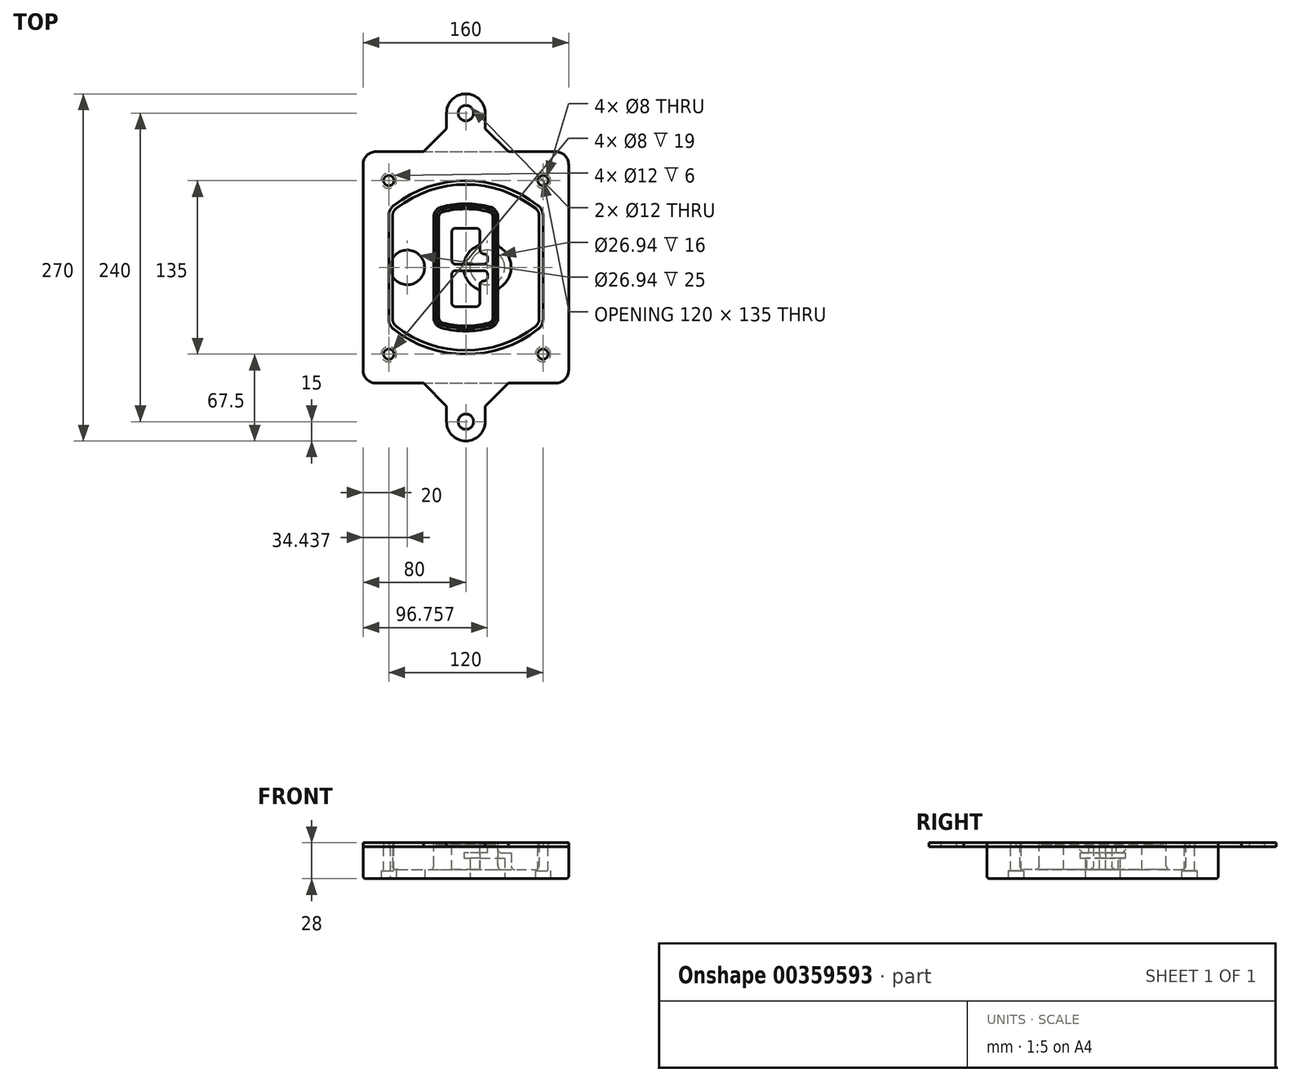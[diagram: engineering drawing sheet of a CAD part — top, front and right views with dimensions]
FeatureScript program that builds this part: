
annotation { "Feature Type Name" : "Feature", "Feature Type Description" : "" }
export const myFeature = defineFeature(function(context is Context, id is Id, definition is map)
    precondition{}
    {
        {
            var Q0;
            Q0=qCreatedBy(makeId("Top.planeOp"),FACE);
            var sketch = newSketch(context, id + "F0", { "sketchPlane" : qUnion([Q0])});
            skPoint(sketch, "E0.rect.middle", {"position": v(0, 0) * mm});
            skLineSegment(sketch, "E1.bottom", {"start": v(-70, -90) * mm, "end": v(70, -90) * mm});
            skLineSegment(sketch, "E1.top", {"start": v(-70, 90) * mm, "end": v(70, 90) * mm});
            skLineSegment(sketch, "E1.left", {"start": v(-80, -80) * mm, "end": v(-80, 80) * mm});
            skLineSegment(sketch, "E1.right", {"start": v(80, -80) * mm, "end": v(80, 80) * mm});
            skLineSegment(sketch, "E2", {"start": v(-80, 90) * mm, "end": v(80, -90) * mm, "construction": true});
            skLineSegment(sketch, "E3", {"start": v(80, 90) * mm, "end": v(-80, -90) * mm, "construction": true});
            skCircle(sketch, "E4", {"center": v(-60, 67.5) * mm, "radius": 4 * mm});
            skCircle(sketch, "E5", {"center": v(60, 67.5) * mm, "radius": 4 * mm});
            skCircle(sketch, "E6", {"center": v(60, -67.5) * mm, "radius": 4 * mm});
            skCircle(sketch, "E7", {"center": v(-60, -67.5) * mm, "radius": 4 * mm});
            skLineSegment(sketch, "E8", {"start": v(-60, 67.5) * mm, "end": v(60, 67.5) * mm, "construction": true});
            skLineSegment(sketch, "E9", {"start": v(60, 67.5) * mm, "end": v(60, -67.5) * mm, "construction": true});
            skLineSegment(sketch, "E10", {"start": v(60, -67.5) * mm, "end": v(-60, -67.5) * mm, "construction": true});
            skLineSegment(sketch, "E11", {"start": v(-60, -67.5) * mm, "end": v(-60, 67.5) * mm, "construction": true});
            skLineSegment(sketch, "E12", {"start": v(-60, 40.3) * mm, "end": v(-60, -40.3) * mm});
            skLineSegment(sketch, "E13", {"start": v(60, 40.3) * mm, "end": v(60, -40.3) * mm});
            skArc(sketch, "E14", {"start": v(56.15, 48.18) * mm, "mid": v(0, 67.5) * mm, "end": v(-56.15, 48.18) * mm});
            skArc(sketch, "E15", {"start": v(-56.15, -48.18) * mm, "mid": v(0, -67.5) * mm, "end": v(56.15, -48.18) * mm});
            skLineSegment(sketch, "E16", {"start": v(-60, 0) * mm, "end": v(60, 0) * mm, "construction": true});
            skPoint(sketch, "E17.visualSharp", {"position": v(-60, -45) * mm});
            skArc(sketch, "E17.filletArc", {"start": v(-60, -40.3) * mm, "mid": v(-58.99, -44.68) * mm, "end": v(-56.15, -48.18) * mm});
            skPoint(sketch, "E18.visualSharp", {"position": v(-60, 45) * mm});
            skArc(sketch, "E18.filletArc", {"start": v(-56.15, 48.18) * mm, "mid": v(-58.99, 44.68) * mm, "end": v(-60, 40.3) * mm});
            skPoint(sketch, "E19.visualSharp", {"position": v(60, 45) * mm});
            skArc(sketch, "E19.filletArc", {"start": v(60, 40.3) * mm, "mid": v(58.99, 44.68) * mm, "end": v(56.15, 48.18) * mm});
            skPoint(sketch, "E20.visualSharp", {"position": v(60, -45) * mm});
            skArc(sketch, "E20.filletArc", {"start": v(56.15, -48.18) * mm, "mid": v(58.99, -44.68) * mm, "end": v(60, -40.3) * mm});
            skPoint(sketch, "E21.visualSharp", {"position": v(-80, 90) * mm});
            skArc(sketch, "E21.filletArc", {"start": v(-70, 90) * mm, "mid": v(-77.07, 87.07) * mm, "end": v(-80, 80) * mm});
            skPoint(sketch, "E22.visualSharp", {"position": v(80, 90) * mm});
            skArc(sketch, "E22.filletArc", {"start": v(80, 80) * mm, "mid": v(77.07, 87.07) * mm, "end": v(70, 90) * mm});
            skPoint(sketch, "E23.visualSharp", {"position": v(80, -90) * mm});
            skArc(sketch, "E23.filletArc", {"start": v(70, -90) * mm, "mid": v(77.07, -87.07) * mm, "end": v(80, -80) * mm});
            skPoint(sketch, "E24.visualSharp", {"position": v(-80, -90) * mm});
            skArc(sketch, "E24.filletArc", {"start": v(-80, -80) * mm, "mid": v(-77.07, -87.07) * mm, "end": v(-70, -90) * mm});
            skArc(sketch, "E25.0", {"start": v(57, 40.3) * mm, "mid": v(56.3, 43.36) * mm, "end": v(54.3, 45.81) * mm});
            skLineSegment(sketch, "E25.1", {"start": v(57, 40.3) * mm, "end": v(57, -40.3) * mm});
            skArc(sketch, "E25.2", {"start": v(54.3, -45.81) * mm, "mid": v(56.3, -43.36) * mm, "end": v(57, -40.3) * mm});
            skArc(sketch, "E25.3", {"start": v(-54.3, -45.81) * mm, "mid": v(0, -64.5) * mm, "end": v(54.3, -45.81) * mm});
            skArc(sketch, "E25.4", {"start": v(-57, -40.3) * mm, "mid": v(-56.3, -43.36) * mm, "end": v(-54.3, -45.81) * mm});
            skArc(sketch, "E25.5", {"start": v(54.3, 45.81) * mm, "mid": v(0, 64.5) * mm, "end": v(-54.3, 45.81) * mm});
            skLineSegment(sketch, "E25.6", {"start": v(-57, 40.3) * mm, "end": v(-57, -40.3) * mm});
            skArc(sketch, "E25.7", {"start": v(-54.3, 45.81) * mm, "mid": v(-56.3, 43.36) * mm, "end": v(-57, 40.3) * mm});
            skArc(sketch, "E26.0", {"start": v(-58.62, 51.33) * mm, "mid": v(-62.58, 46.43) * mm, "end": v(-64, 40.3) * mm});
            skArc(sketch, "E26.1", {"start": v(58.62, 51.33) * mm, "mid": v(0, 71.5) * mm, "end": v(-58.62, 51.33) * mm});
            skArc(sketch, "E26.2", {"start": v(64, 40.3) * mm, "mid": v(62.58, 46.43) * mm, "end": v(58.62, 51.33) * mm});
            skLineSegment(sketch, "E26.3", {"start": v(64, 40.3) * mm, "end": v(64, -40.3) * mm});
            skArc(sketch, "E26.4", {"start": v(58.62, -51.33) * mm, "mid": v(62.58, -46.43) * mm, "end": v(64, -40.3) * mm});
            skLineSegment(sketch, "E26.5", {"start": v(-64, 40.3) * mm, "end": v(-64, -40.3) * mm});
            skArc(sketch, "E26.6", {"start": v(-58.62, -51.33) * mm, "mid": v(0, -71.5) * mm, "end": v(58.62, -51.33) * mm});
            skArc(sketch, "E26.7", {"start": v(-64, -40.3) * mm, "mid": v(-62.58, -46.43) * mm, "end": v(-58.62, -51.33) * mm});
            skSolve(sketch);
        }
        {
            var Q0;
            Q0=makeQuery(id+"F0.imprint","IMPRINT",FACE,{"disambiguationData":[TD([[makeQuery(id+"F0.imprint","IMPRINT",EDGE,{"derivedFrom":sQuery(id+"F0.wireOp",EDGE,"E1.bottom")}),1.0]])]});
            var Q1;
            Q1=makeQuery(id+"F0.imprint","IMPRINT",FACE,{"disambiguationData":[TD([[makeQuery(id+"F0.imprint","IMPRINT",EDGE,{"derivedFrom":sQuery(id+"F0.wireOp",EDGE,"E12")}),1.0]])]});
            var Q2;
            Q2=makeQuery(id+"F0.imprint","IMPRINT",FACE,{"disambiguationData":[TD([[makeQuery(id+"F0.imprint","IMPRINT",EDGE,{"derivedFrom":sQuery(id+"F0.wireOp",EDGE,"E25.0")}),1.0]])]});
            var Q3;
            Q3=makeQuery(id+"F0.imprint","IMPRINT",FACE,{"disambiguationData":[TD([[makeQuery(id+"F0.imprint","IMPRINT",EDGE,{"derivedFrom":sQuery(id+"F0.wireOp",EDGE,"E12")}),-1.0]])]});
            extrude(context, id + "F1", {"entities" : qUnion([Q0, Q1, Q2, Q3]), "oppositeDirection" : true, "depth" : 25 * mm});
        }
        {
            var Q0;
            Q0=makeQuery(id+"F0.imprint","IMPRINT",FACE,{"disambiguationData":[TD([[makeQuery(id+"F0.imprint","IMPRINT",EDGE,{"derivedFrom":sQuery(id+"F0.wireOp",EDGE,"E12")}),1.0]])]});
            extrude(context, id + "F2", {"entities" : qUnion([Q0]), "operationType" : NewBodyOperationType.ADD, "depth" : 3 * mm});
        }
        {
            var Q0;
            Q0=makeQuery(id+"F0.imprint","IMPRINT",FACE,{"disambiguationData":[TD([[makeQuery(id+"F0.imprint","IMPRINT",EDGE,{"derivedFrom":sQuery(id+"F0.wireOp",EDGE,"E25.0")}),1.0]])]});
            extrude(context, id + "F3", {"entities" : qUnion([Q0]), "operationType" : NewBodyOperationType.REMOVE, "oppositeDirection" : true, "depth" : 18 * mm});
        }
        {
            var Q0;
            Q0=makeQuery(id+"F2.opExtrude","CAP_FACE",FACE,{"disambiguationData":[OSD([sQuery(id+"F0.wireOp",EDGE,"E12"),sQuery(id+"F0.wireOp",EDGE,"E13"),sQuery(id+"F0.wireOp",EDGE,"E14"),sQuery(id+"F0.wireOp",EDGE,"E15"),sQuery(id+"F0.wireOp",EDGE,"E17.filletArc"),sQuery(id+"F0.wireOp",EDGE,"E18.filletArc"),sQuery(id+"F0.wireOp",EDGE,"E19.filletArc"),sQuery(id+"F0.wireOp",EDGE,"E20.filletArc"),sQuery(id+"F0.wireOp",EDGE,"E25.0"),sQuery(id+"F0.wireOp",EDGE,"E25.1"),sQuery(id+"F0.wireOp",EDGE,"E25.2"),sQuery(id+"F0.wireOp",EDGE,"E25.3"),sQuery(id+"F0.wireOp",EDGE,"E25.4"),sQuery(id+"F0.wireOp",EDGE,"E25.5"),sQuery(id+"F0.wireOp",EDGE,"E25.6"),sQuery(id+"F0.wireOp",EDGE,"E25.7")])],"isStart":false});
            var sketch = newSketch(context, id + "F4", { "sketchPlane" : qUnion([Q0])});
            skArc(sketch, "E27.0", {"start": v(-19.08, -46.97) * mm, "mid": v(0, -49.5) * mm, "end": v(19.08, -46.97) * mm});
            skArc(sketch, "E28.0", {"start": v(19.08, 46.97) * mm, "mid": v(0, 49.5) * mm, "end": v(-19.08, 46.97) * mm});
            skLineSegment(sketch, "E29", {"start": v(-25, 39.25) * mm, "end": v(-25, -39.25) * mm});
            skLineSegment(sketch, "E30", {"start": v(25, 39.25) * mm, "end": v(25, -39.25) * mm});
            skLineSegment(sketch, "E31", {"start": v(-25, 45.1) * mm, "end": v(25, 45.1) * mm, "construction": true});
            skLineSegment(sketch, "E32", {"start": v(-25, -45.1) * mm, "end": v(25, -45.1) * mm, "construction": true});
            skPoint(sketch, "E33.visualSharp", {"position": v(-25, 45.1) * mm});
            skArc(sketch, "E33.filletArc", {"start": v(-19.08, 46.97) * mm, "mid": v(-23.35, 44.11) * mm, "end": v(-25, 39.25) * mm});
            skPoint(sketch, "E34.visualSharp", {"position": v(25, 45.1) * mm});
            skArc(sketch, "E34.filletArc", {"start": v(25, 39.25) * mm, "mid": v(23.35, 44.11) * mm, "end": v(19.08, 46.97) * mm});
            skPoint(sketch, "E35.visualSharp", {"position": v(25, -45.1) * mm});
            skArc(sketch, "E35.filletArc", {"start": v(19.08, -46.97) * mm, "mid": v(23.35, -44.11) * mm, "end": v(25, -39.25) * mm});
            skPoint(sketch, "E36.visualSharp", {"position": v(-25, -45.1) * mm});
            skArc(sketch, "E36.filletArc", {"start": v(-25, -39.25) * mm, "mid": v(-23.35, -44.11) * mm, "end": v(-19.08, -46.97) * mm});
            skArc(sketch, "E37.0", {"start": v(54.3, 45.81) * mm, "mid": v(0, 64.5) * mm, "end": v(-54.3, 45.81) * mm});
            skArc(sketch, "E37.1", {"start": v(-54.3, 45.81) * mm, "mid": v(-56.3, 43.36) * mm, "end": v(-57, 40.3) * mm});
            skLineSegment(sketch, "E37.2", {"start": v(-57, 40.3) * mm, "end": v(-57, -40.3) * mm});
            skArc(sketch, "E37.3", {"start": v(-57, -40.3) * mm, "mid": v(-56.3, -43.36) * mm, "end": v(-54.3, -45.81) * mm});
            skArc(sketch, "E37.4", {"start": v(-54.3, -45.81) * mm, "mid": v(0, -64.5) * mm, "end": v(54.3, -45.81) * mm});
            skArc(sketch, "E37.5", {"start": v(54.3, -45.81) * mm, "mid": v(56.3, -43.36) * mm, "end": v(57, -40.3) * mm});
            skLineSegment(sketch, "E37.6", {"start": v(57, 40.3) * mm, "end": v(57, -40.3) * mm});
            skArc(sketch, "E37.7", {"start": v(57, 40.3) * mm, "mid": v(56.3, 43.36) * mm, "end": v(54.3, 45.81) * mm});
            skLineSegment(sketch, "E38.0", {"start": v(23, 39.25) * mm, "end": v(23, -39.25) * mm});
            skArc(sketch, "E38.1", {"start": v(18.56, -45.04) * mm, "mid": v(21.76, -42.9) * mm, "end": v(23, -39.25) * mm});
            skArc(sketch, "E38.2", {"start": v(-18.56, -45.04) * mm, "mid": v(0, -47.5) * mm, "end": v(18.56, -45.04) * mm});
            skArc(sketch, "E38.3", {"start": v(-23, -39.25) * mm, "mid": v(-21.76, -42.9) * mm, "end": v(-18.56, -45.04) * mm});
            skLineSegment(sketch, "E38.4", {"start": v(-23, 39.25) * mm, "end": v(-23, -39.25) * mm});
            skArc(sketch, "E38.5", {"start": v(23, 39.25) * mm, "mid": v(21.76, 42.9) * mm, "end": v(18.56, 45.04) * mm});
            skArc(sketch, "E38.6", {"start": v(-18.56, 45.04) * mm, "mid": v(-21.76, 42.9) * mm, "end": v(-23, 39.25) * mm});
            skArc(sketch, "E38.7", {"start": v(18.56, 45.04) * mm, "mid": v(0, 47.5) * mm, "end": v(-18.56, 45.04) * mm});
            skArc(sketch, "E39.0", {"start": v(21, 39.25) * mm, "mid": v(20.18, 41.68) * mm, "end": v(18.04, 43.1) * mm});
            skLineSegment(sketch, "E39.1", {"start": v(21, 39.25) * mm, "end": v(21, -39.25) * mm});
            skArc(sketch, "E39.2", {"start": v(18.04, -43.1) * mm, "mid": v(20.18, -41.68) * mm, "end": v(21, -39.25) * mm});
            skArc(sketch, "E39.3", {"start": v(-18.04, -43.1) * mm, "mid": v(0, -45.5) * mm, "end": v(18.04, -43.1) * mm});
            skArc(sketch, "E39.4", {"start": v(-21, -39.25) * mm, "mid": v(-20.18, -41.68) * mm, "end": v(-18.04, -43.1) * mm});
            skArc(sketch, "E39.5", {"start": v(18.04, 43.1) * mm, "mid": v(0, 45.5) * mm, "end": v(-18.04, 43.1) * mm});
            skLineSegment(sketch, "E39.6", {"start": v(-21, 39.25) * mm, "end": v(-21, -39.25) * mm});
            skArc(sketch, "E39.7", {"start": v(-18.04, 43.1) * mm, "mid": v(-20.18, 41.68) * mm, "end": v(-21, 39.25) * mm});
            skLineSegment(sketch, "E40", {"start": v(-25, 0) * mm, "end": v(25, 0) * mm, "construction": true});
            skLineSegment(sketch, "E41", {"start": v(-11, 5.5) * mm, "end": v(-11, 27.5) * mm});
            skLineSegment(sketch, "E42", {"start": v(-8, 30.5) * mm, "end": v(8, 30.5) * mm});
            skLineSegment(sketch, "E43", {"start": v(11, 27.5) * mm, "end": v(11, 13.5) * mm});
            skLineSegment(sketch, "E44", {"start": v(14, 10.5) * mm, "end": v(14, 10.5) * mm});
            skLineSegment(sketch, "E45", {"start": v(17, 7.5) * mm, "end": v(17, 5.5) * mm});
            skLineSegment(sketch, "E46", {"start": v(14, 2.5) * mm, "end": v(-8, 2.5) * mm});
            skPoint(sketch, "E47.visualSharp", {"position": v(-11, 30.5) * mm});
            skArc(sketch, "E47.filletArc", {"start": v(-8, 30.5) * mm, "mid": v(-10.12, 29.62) * mm, "end": v(-11, 27.5) * mm});
            skPoint(sketch, "E48.visualSharp", {"position": v(11, 30.5) * mm});
            skArc(sketch, "E48.filletArc", {"start": v(11, 27.5) * mm, "mid": v(10.12, 29.62) * mm, "end": v(8, 30.5) * mm});
            skPoint(sketch, "E49.visualSharp", {"position": v(11, 10.5) * mm});
            skArc(sketch, "E49.filletArc", {"start": v(11, 13.5) * mm, "mid": v(11.88, 11.38) * mm, "end": v(14, 10.5) * mm});
            skPoint(sketch, "E50.visualSharp", {"position": v(17, 10.5) * mm});
            skArc(sketch, "E50.filletArc", {"start": v(17, 7.5) * mm, "mid": v(16.12, 9.62) * mm, "end": v(14, 10.5) * mm});
            skPoint(sketch, "E51.visualSharp", {"position": v(17, 2.5) * mm});
            skArc(sketch, "E51.filletArc", {"start": v(14, 2.5) * mm, "mid": v(16.12, 3.38) * mm, "end": v(17, 5.5) * mm});
            skPoint(sketch, "E52.visualSharp", {"position": v(-11, 2.5) * mm});
            skArc(sketch, "E52.filletArc", {"start": v(-11, 5.5) * mm, "mid": v(-10.12, 3.38) * mm, "end": v(-8, 2.5) * mm});
            skLineSegment(sketch, "E53.0.MirrorCS", {"start": v(14, -2.5) * mm, "end": v(-8, -2.5) * mm});
            skArc(sketch, "E54.0.MirrorCS", {"start": v(-11, -5.5) * mm, "mid": v(-10.12, -3.38) * mm, "end": v(-8, -2.5) * mm});
            skLineSegment(sketch, "E55.0.MirrorCS", {"start": v(-11, -5.5) * mm, "end": v(-11, -27.5) * mm});
            skArc(sketch, "E56.0.MirrorCS", {"start": v(-8, -30.5) * mm, "mid": v(-10.12, -29.62) * mm, "end": v(-11, -27.5) * mm});
            skLineSegment(sketch, "E57.0.MirrorCS", {"start": v(-8, -30.5) * mm, "end": v(8, -30.5) * mm});
            skArc(sketch, "E58.0.MirrorCS", {"start": v(11, -27.5) * mm, "mid": v(10.12, -29.62) * mm, "end": v(8, -30.5) * mm});
            skLineSegment(sketch, "E59.0.MirrorCS", {"start": v(11, -27.5) * mm, "end": v(11, -13.5) * mm});
            skArc(sketch, "E60.0.MirrorCS", {"start": v(11, -13.5) * mm, "mid": v(11.88, -11.38) * mm, "end": v(14, -10.5) * mm});
            skArc(sketch, "E61.0.MirrorCS", {"start": v(17, -7.5) * mm, "mid": v(16.12, -9.62) * mm, "end": v(14, -10.5) * mm});
            skLineSegment(sketch, "E62.0.MirrorCS", {"start": v(17, -7.5) * mm, "end": v(17, -5.5) * mm});
            skArc(sketch, "E63.0.MirrorCS", {"start": v(14, -2.5) * mm, "mid": v(16.12, -3.38) * mm, "end": v(17, -5.5) * mm});
            skSolve(sketch);
        }
        {
            var Q0;
            Q0=makeQuery(id+"F4.imprint","IMPRINT",FACE,{"disambiguationData":[TD([[makeQuery(id+"F4.imprint","IMPRINT",EDGE,{"derivedFrom":sQuery(id+"F4.wireOp",EDGE,"E27.0")}),1.0]])]});
            var Q1;
            Q1=makeQuery(id+"F4.imprint","IMPRINT",FACE,{"disambiguationData":[TD([[makeQuery(id+"F4.imprint","IMPRINT",EDGE,{"derivedFrom":sQuery(id+"F4.wireOp",EDGE,"E38.0")}),-1.0]])]});
            var Q2;
            Q2=makeQuery(id+"F4.imprint","IMPRINT",FACE,{"disambiguationData":[TD([[makeQuery(id+"F4.imprint","IMPRINT",EDGE,{"derivedFrom":sQuery(id+"F4.wireOp",EDGE,"E39.0")}),1.0]])]});
            extrude(context, id + "F5", {"entities" : qUnion([Q0, Q1, Q2]), "operationType" : NewBodyOperationType.ADD, "endBound" : BoundingType.UP_TO_NEXT, "oppositeDirection" : true, "depth" : 25 * mm});
        }
        {
            var Q0;
            Q0=makeQuery(id+"F4.imprint","IMPRINT",FACE,{"disambiguationData":[TD([[makeQuery(id+"F4.imprint","IMPRINT",EDGE,{"derivedFrom":sQuery(id+"F4.wireOp",EDGE,"E38.0")}),-1.0]])]});
            extrude(context, id + "F6", {"entities" : qUnion([Q0]), "operationType" : NewBodyOperationType.REMOVE, "oppositeDirection" : true, "depth" : 2 * mm});
        }
        {
            var Q0;
            Q0=makeQuery(id+"F1.opExtrude","CAP_FACE",FACE,{"disambiguationData":[OSD([sQuery(id+"F0.wireOp",EDGE,"E1.bottom"),sQuery(id+"F0.wireOp",EDGE,"E1.top"),sQuery(id+"F0.wireOp",EDGE,"E1.left"),sQuery(id+"F0.wireOp",EDGE,"E1.right"),sQuery(id+"F0.wireOp",EDGE,"E4"),sQuery(id+"F0.wireOp",EDGE,"E5"),sQuery(id+"F0.wireOp",EDGE,"E6"),sQuery(id+"F0.wireOp",EDGE,"E7"),sQuery(id+"F0.wireOp",EDGE,"E21.filletArc"),sQuery(id+"F0.wireOp",EDGE,"E22.filletArc"),sQuery(id+"F0.wireOp",EDGE,"E23.filletArc"),sQuery(id+"F0.wireOp",EDGE,"E24.filletArc")])],"isStart":false});
            var sketch = newSketch(context, id + "F7", { "sketchPlane" : qUnion([Q0])});
            skCircle(sketch, "E64", {"center": v(16.76, 0) * mm, "radius": 13.47 * mm});
            skCircle(sketch, "E65", {"center": v(-45.56, 0) * mm, "radius": 13.47 * mm});
            skLineSegment(sketch, "E66", {"start": v(80, 0) * mm, "end": v(-80, 0) * mm});
            skCircle(sketch, "E67", {"center": v(16.76, 0) * mm, "radius": 18.47 * mm});
            skCircle(sketch, "E68", {"center": v(60, -67.5) * mm, "radius": 6 * mm});
            skCircle(sketch, "E69", {"center": v(-60, -67.5) * mm, "radius": 6 * mm});
            skCircle(sketch, "E70", {"center": v(-60, 67.5) * mm, "radius": 6 * mm});
            skCircle(sketch, "E71", {"center": v(60, 67.5) * mm, "radius": 6 * mm});
            skSolve(sketch);
        }
        {
            var Q0;
            {var subQ1=sQuery(id+"F7.wireOp",EDGE,"E66");var subQ4=sQuery(id+"F7.wireOp",EDGE,"E64");var subQ6=makeQuery(id+"F7.imprint","INTERSECT",VERTEX,{"disambiguationData":[OD(0.0)],"derivedFrom":[subQ4,subQ1]});Q0=makeQuery(id+"F7.imprint","IMPRINT",FACE,{"disambiguationData":[TD([[makeQuery(id+"F7.imprint","IMPRINT",EDGE,{"disambiguationData":[TD([[subQ6,-1.0]])],"derivedFrom":subQ4}),-1.0]])]});}
            var Q1;
            {var subQ0=sQuery(id+"F7.wireOp",EDGE,"E66");var subQ1=sQuery(id+"F7.wireOp",EDGE,"E64");var subQ3=makeQuery(id+"F7.imprint","INTERSECT",VERTEX,{"disambiguationData":[OD(0.0)],"derivedFrom":[subQ1,subQ0]});Q1=makeQuery(id+"F7.imprint","IMPRINT",FACE,{"disambiguationData":[TD([[makeQuery(id+"F7.imprint","IMPRINT",EDGE,{"disambiguationData":[TD([[subQ3,-1.0]])],"derivedFrom":subQ1}),1.0]])]});}
            var Q2;
            {var subQ0=sQuery(id+"F7.wireOp",EDGE,"E66");var subQ1=sQuery(id+"F7.wireOp",EDGE,"E64");var subQ3=makeQuery(id+"F7.imprint","INTERSECT",VERTEX,{"disambiguationData":[OD(0.0)],"derivedFrom":[subQ1,subQ0]});Q2=makeQuery(id+"F7.imprint","IMPRINT",FACE,{"disambiguationData":[TD([[makeQuery(id+"F7.imprint","IMPRINT",EDGE,{"disambiguationData":[TD([[subQ3,1.0]])],"derivedFrom":subQ1}),1.0]])]});}
            var Q3;
            {var subQ1=sQuery(id+"F7.wireOp",EDGE,"E66");var subQ4=sQuery(id+"F7.wireOp",EDGE,"E64");var subQ6=makeQuery(id+"F7.imprint","INTERSECT",VERTEX,{"disambiguationData":[OD(0.0)],"derivedFrom":[subQ4,subQ1]});Q3=makeQuery(id+"F7.imprint","IMPRINT",FACE,{"disambiguationData":[TD([[makeQuery(id+"F7.imprint","IMPRINT",EDGE,{"disambiguationData":[TD([[subQ6,1.0]])],"derivedFrom":subQ4}),-1.0]])]});}
            extrude(context, id + "F8", {"entities" : qUnion([Q0, Q1, Q2, Q3]), "operationType" : NewBodyOperationType.ADD, "oppositeDirection" : true, "depth" : 20 * mm});
        }
        {
            var Q0;
            {var subQ0=sQuery(id+"F7.wireOp",EDGE,"E66");var subQ1=sQuery(id+"F7.wireOp",EDGE,"E64");var subQ3=makeQuery(id+"F7.imprint","INTERSECT",VERTEX,{"disambiguationData":[OD(0.0)],"derivedFrom":[subQ1,subQ0]});Q0=makeQuery(id+"F7.imprint","IMPRINT",FACE,{"disambiguationData":[TD([[makeQuery(id+"F7.imprint","IMPRINT",EDGE,{"disambiguationData":[TD([[subQ3,-1.0]])],"derivedFrom":subQ1}),1.0]])]});}
            var Q1;
            {var subQ0=sQuery(id+"F7.wireOp",EDGE,"E66");var subQ1=sQuery(id+"F7.wireOp",EDGE,"E64");var subQ3=makeQuery(id+"F7.imprint","INTERSECT",VERTEX,{"disambiguationData":[OD(0.0)],"derivedFrom":[subQ1,subQ0]});Q1=makeQuery(id+"F7.imprint","IMPRINT",FACE,{"disambiguationData":[TD([[makeQuery(id+"F7.imprint","IMPRINT",EDGE,{"disambiguationData":[TD([[subQ3,1.0]])],"derivedFrom":subQ1}),1.0]])]});}
            extrude(context, id + "F9", {"entities" : qUnion([Q0, Q1]), "operationType" : NewBodyOperationType.REMOVE, "oppositeDirection" : true, "depth" : 16 * mm});
        }
        {
            var Q0;
            {var subQ0=sQuery(id+"F7.wireOp",EDGE,"E66");var subQ1=sQuery(id+"F7.wireOp",EDGE,"E65");var subQ3=makeQuery(id+"F7.imprint","INTERSECT",VERTEX,{"disambiguationData":[OD(0.0)],"derivedFrom":[subQ1,subQ0]});Q0=makeQuery(id+"F7.imprint","IMPRINT",FACE,{"disambiguationData":[TD([[makeQuery(id+"F7.imprint","IMPRINT",EDGE,{"disambiguationData":[TD([[subQ3,-1.0]])],"derivedFrom":subQ1}),1.0]])]});}
            var Q1;
            {var subQ0=sQuery(id+"F7.wireOp",EDGE,"E66");var subQ1=sQuery(id+"F7.wireOp",EDGE,"E65");var subQ3=makeQuery(id+"F7.imprint","INTERSECT",VERTEX,{"disambiguationData":[OD(0.0)],"derivedFrom":[subQ1,subQ0]});Q1=makeQuery(id+"F7.imprint","IMPRINT",FACE,{"disambiguationData":[TD([[makeQuery(id+"F7.imprint","IMPRINT",EDGE,{"disambiguationData":[TD([[subQ3,1.0]])],"derivedFrom":subQ1}),1.0]])]});}
            extrude(context, id + "F10", {"entities" : qUnion([Q0, Q1]), "operationType" : NewBodyOperationType.REMOVE, "oppositeDirection" : true, "depth" : 25 * mm});
        }
        {
            var Q0;
            Q0=makeQuery(id+"F7.imprint","IMPRINT",FACE,{"disambiguationData":[TD([[makeQuery(id+"F7.imprint","IMPRINT",EDGE,{"derivedFrom":sQuery(id+"F7.wireOp",EDGE,"E68")}),1.0]])]});
            var Q1;
            Q1=makeQuery(id+"F7.imprint","IMPRINT",FACE,{"disambiguationData":[TD([[makeQuery(id+"F7.imprint","IMPRINT",EDGE,{"derivedFrom":makeQuery(id+"F1.opExtrude","CAP_EDGE",EDGE,{"disambiguationData":[OSD([sQuery(id+"F0.wireOp",EDGE,"E5")])],"isStart":false})}),-1.0]])]});
            var Q2;
            Q2=makeQuery(id+"F7.imprint","IMPRINT",FACE,{"disambiguationData":[TD([[makeQuery(id+"F7.imprint","IMPRINT",EDGE,{"derivedFrom":sQuery(id+"F7.wireOp",EDGE,"E69")}),1.0]])]});
            var Q3;
            Q3=makeQuery(id+"F7.imprint","IMPRINT",FACE,{"disambiguationData":[TD([[makeQuery(id+"F7.imprint","IMPRINT",EDGE,{"derivedFrom":makeQuery(id+"F1.opExtrude","CAP_EDGE",EDGE,{"disambiguationData":[OSD([sQuery(id+"F0.wireOp",EDGE,"E4")])],"isStart":false})}),-1.0]])]});
            var Q4;
            Q4=makeQuery(id+"F7.imprint","IMPRINT",FACE,{"disambiguationData":[TD([[makeQuery(id+"F7.imprint","IMPRINT",EDGE,{"derivedFrom":sQuery(id+"F7.wireOp",EDGE,"E70")}),1.0]])]});
            var Q5;
            Q5=makeQuery(id+"F7.imprint","IMPRINT",FACE,{"disambiguationData":[TD([[makeQuery(id+"F7.imprint","IMPRINT",EDGE,{"derivedFrom":makeQuery(id+"F1.opExtrude","CAP_EDGE",EDGE,{"disambiguationData":[OSD([sQuery(id+"F0.wireOp",EDGE,"E7")])],"isStart":false})}),-1.0]])]});
            var Q6;
            Q6=makeQuery(id+"F7.imprint","IMPRINT",FACE,{"disambiguationData":[TD([[makeQuery(id+"F7.imprint","IMPRINT",EDGE,{"derivedFrom":sQuery(id+"F7.wireOp",EDGE,"E71")}),1.0]])]});
            var Q7;
            Q7=makeQuery(id+"F7.imprint","IMPRINT",FACE,{"disambiguationData":[TD([[makeQuery(id+"F7.imprint","IMPRINT",EDGE,{"derivedFrom":makeQuery(id+"F1.opExtrude","CAP_EDGE",EDGE,{"disambiguationData":[OSD([sQuery(id+"F0.wireOp",EDGE,"E6")])],"isStart":false})}),-1.0]])]});
            extrude(context, id + "F11", {"entities" : qUnion([Q0, Q1, Q2, Q3, Q4, Q5, Q6, Q7]), "operationType" : NewBodyOperationType.REMOVE, "oppositeDirection" : true, "depth" : 6 * mm});
        }
        {
            var Q0;
            Q0=makeQuery(id+"F9.boolean.opBoolean","COPY",FACE,{"derivedFrom":makeQuery(id+"F9.opExtrude","CAP_FACE",FACE,{"disambiguationData":[OSD([sQuery(id+"F7.wireOp",EDGE,"E64")])],"isStart":false})});
            var sketch = newSketch(context, id + "F12", { "sketchPlane" : qUnion([Q0])});
            skArc(sketch, "E72.0", {"start": v(11, 17.55) * mm, "mid": v(2.57, 11.82) * mm, "end": v(-1.54, 2.5) * mm});
            skArc(sketch, "E72.1", {"start": v(-1.54, -2.5) * mm, "mid": v(2.57, -11.82) * mm, "end": v(11, -17.55) * mm});
            skLineSegment(sketch, "E73", {"start": v(-1.54, -2.5) * mm, "end": v(14, -2.5) * mm});
            skLineSegment(sketch, "E74.0", {"start": v(14, 2.5) * mm, "end": v(-1.54, 2.5) * mm});
            skArc(sketch, "E74.1", {"start": v(14, 2.5) * mm, "mid": v(16.12, 3.38) * mm, "end": v(17, 5.5) * mm});
            skLineSegment(sketch, "E74.2", {"start": v(17, 7.5) * mm, "end": v(17, 5.5) * mm});
            skArc(sketch, "E74.3", {"start": v(17, 7.5) * mm, "mid": v(16.12, 9.62) * mm, "end": v(14, 10.5) * mm});
            skArc(sketch, "E74.4", {"start": v(11, 13.5) * mm, "mid": v(11.88, 11.38) * mm, "end": v(14, 10.5) * mm});
            skLineSegment(sketch, "E74.5", {"start": v(11, 17.55) * mm, "end": v(11, 13.5) * mm});
            skLineSegment(sketch, "E74.7", {"start": v(14, -2.5) * mm, "end": v(-1.54, -2.5) * mm});
            skArc(sketch, "E74.8", {"start": v(14, -2.5) * mm, "mid": v(16.12, -3.38) * mm, "end": v(17, -5.5) * mm});
            skLineSegment(sketch, "E74.9", {"start": v(17, -7.5) * mm, "end": v(17, -5.5) * mm});
            skArc(sketch, "E74.10", {"start": v(17, -7.5) * mm, "mid": v(16.12, -9.62) * mm, "end": v(14, -10.5) * mm});
            skArc(sketch, "E74.11", {"start": v(11, -13.5) * mm, "mid": v(11.88, -11.38) * mm, "end": v(14, -10.5) * mm});
            skLineSegment(sketch, "E74.12", {"start": v(11, -17.55) * mm, "end": v(11, -13.5) * mm});
            skPoint(sketch, "E75.orphan", {"position": v(11, -27.5) * mm});
            skPoint(sketch, "E76.orphan", {"position": v(-8, -2.5) * mm});
            skPoint(sketch, "E77.orphan", {"position": v(-8, 2.5) * mm});
            skPoint(sketch, "E78.orphan", {"position": v(11, 27.5) * mm});
            skSolve(sketch);
        }
        {
            var Q0;
            {var subQ7=sQuery(id+"F12.wireOp",EDGE,"E72.0");var subQ14=sQuery(id+"F12.wireOp",EDGE,"E72.1");var subQ16=sQuery(id+"F12.wireOp",EDGE,"E74.1");var subQ18=sQuery(id+"F12.wireOp",EDGE,"E74.8");Q0=qUnion([makeQuery(id+"F12.imprint","IMPRINT",FACE,{"disambiguationData":[TD([[makeQuery(id+"F12.imprint","IMPRINT",EDGE,{"derivedFrom":subQ7}),1.0]])]}),makeQuery(id+"F12.imprint","IMPRINT",FACE,{"disambiguationData":[TD([[makeQuery(id+"F12.imprint","IMPRINT",EDGE,{"derivedFrom":subQ14}),1.0]])]}),makeQuery(id+"F12.imprint","IMPRINT",FACE,{"disambiguationData":[TD([[makeQuery(id+"F12.imprint","IMPRINT",EDGE,{"derivedFrom":subQ16}),1.0]])]}),makeQuery(id+"F12.imprint","IMPRINT",FACE,{"disambiguationData":[TD([[makeQuery(id+"F12.imprint","IMPRINT",EDGE,{"derivedFrom":subQ18}),-1.0]])]})]);}
            var Q1;
            Q1=makeQuery(id+"F5.boolean.opBoolean","SPLIT",FACE,{"disambiguationData":[TD([makeQuery(id+"F5.opExtrude","SWEPT_FACE",FACE,{"disambiguationData":[OSD([sQuery(id+"F4.wireOp",EDGE,"E41")])]})])],"derivedFrom":makeQuery(id+"F3.boolean.opBoolean","COPY",FACE,{"derivedFrom":makeQuery(id+"F3.opExtrude","CAP_FACE",FACE,{"disambiguationData":[OSD([sQuery(id+"F0.wireOp",EDGE,"E25.0"),sQuery(id+"F0.wireOp",EDGE,"E25.1"),sQuery(id+"F0.wireOp",EDGE,"E25.2"),sQuery(id+"F0.wireOp",EDGE,"E25.3"),sQuery(id+"F0.wireOp",EDGE,"E25.4"),sQuery(id+"F0.wireOp",EDGE,"E25.5"),sQuery(id+"F0.wireOp",EDGE,"E25.6"),sQuery(id+"F0.wireOp",EDGE,"E25.7")])],"isStart":false})})});
            extrude(context, id + "F13", {"entities" : qUnion([Q0]), "operationType" : NewBodyOperationType.REMOVE, "endBound" : BoundingType.UP_TO_SURFACE, "endBoundEntityFace" : qUnion([Q1]), "depth" : 25 * mm});
        }
        {
            var Q0;
            Q0=makeQuery(id+"F3.boolean.opBoolean","COPY",EDGE,{"derivedFrom":makeQuery(id+"F3.opExtrude","CAP_EDGE",EDGE,{"disambiguationData":[OSD([sQuery(id+"F0.wireOp",EDGE,"E25.6")])],"isStart":false})});
            var Q1;
            Q1=makeQuery(id+"F8.boolean.opBoolean","INTERSECT",EDGE,{"derivedFrom":[makeQuery(id+"F5.opExtrude","SWEPT_FACE",FACE,{"disambiguationData":[OSD([sQuery(id+"F4.wireOp",EDGE,"E30")])]}),makeQuery(id+"F8.opExtrude","CAP_FACE",FACE,{"disambiguationData":[OSD([sQuery(id+"F7.wireOp",EDGE,"E67")])],"isStart":false})]});
            var Q2;
            Q2=makeQuery(id+"F8.boolean.opBoolean","INTERSECT",EDGE,{"disambiguationData":[OD(1.0)],"derivedFrom":[makeQuery(id+"F5.opExtrude","SWEPT_FACE",FACE,{"disambiguationData":[OSD([sQuery(id+"F4.wireOp",EDGE,"E30")])]}),makeQuery(id+"F8.opExtrude","SWEPT_FACE",FACE,{"disambiguationData":[OSD([sQuery(id+"F7.wireOp",EDGE,"E67")])]})]});
            var Q3;
            {var subQ0=sQuery(id+"F4.wireOp",EDGE,"E30");Q3=makeQuery(id+"F8.boolean.opBoolean","SPLIT",EDGE,{"disambiguationData":[TD([makeQuery(id+"F5.opExtrude","SWEPT_FACE",FACE,{"disambiguationData":[OSD([sQuery(id+"F4.wireOp",EDGE,"E35.filletArc")])]})])],"derivedFrom":makeQuery(id+"F5.opExtrude","CAP_EDGE",EDGE,{"disambiguationData":[OSD([subQ0])],"isStart":false})});}
            var Q4;
            {var subQ0=sQuery(id+"F0.wireOp",EDGE,"E25.7");var subQ1=sQuery(id+"F0.wireOp",EDGE,"E25.1");var subQ2=sQuery(id+"F0.wireOp",EDGE,"E25.6");var subQ3=sQuery(id+"F0.wireOp",EDGE,"E25.5");var subQ4=sQuery(id+"F0.wireOp",EDGE,"E25.4");var subQ5=sQuery(id+"F0.wireOp",EDGE,"E25.0");var subQ6=sQuery(id+"F0.wireOp",EDGE,"E25.2");var subQ7=sQuery(id+"F0.wireOp",EDGE,"E25.3");Q4=makeQuery(id+"F8.boolean.opBoolean","INTERSECT",EDGE,{"derivedFrom":[makeQuery(id+"F5.boolean.opBoolean","SPLIT",FACE,{"disambiguationData":[TD([makeQuery(id+"F2.opExtrude","SWEPT_FACE",FACE,{"disambiguationData":[OSD([subQ5])]})])],"derivedFrom":makeQuery(id+"F3.boolean.opBoolean","COPY",FACE,{"derivedFrom":makeQuery(id+"F3.opExtrude","CAP_FACE",FACE,{"disambiguationData":[OSD([subQ5,subQ1,subQ6,subQ7,subQ4,subQ3,subQ2,subQ0])],"isStart":false})})}),makeQuery(id+"F8.opExtrude","SWEPT_FACE",FACE,{"disambiguationData":[OSD([sQuery(id+"F7.wireOp",EDGE,"E67")])]})]});}
            var Q5;
            Q5=makeQuery(id+"F8.boolean.opBoolean","INTERSECT",EDGE,{"disambiguationData":[OD(0.0)],"derivedFrom":[makeQuery(id+"F5.opExtrude","SWEPT_FACE",FACE,{"disambiguationData":[OSD([sQuery(id+"F4.wireOp",EDGE,"E30")])]}),makeQuery(id+"F8.opExtrude","SWEPT_FACE",FACE,{"disambiguationData":[OSD([sQuery(id+"F7.wireOp",EDGE,"E67")])]})]});
            fillet(context, id + "F14", {"entities" : qUnion([Q0, Q1, Q2, Q3, Q4, Q5]), "radius" : 3 * mm, "tangentPropagation" : true, "allowEdgeOverflow" : false});
        }
        {
            var Q0;
            Q0=makeQuery(id+"F1.opExtrude","CAP_EDGE",EDGE,{"disambiguationData":[OSD([sQuery(id+"F0.wireOp",EDGE,"E1.bottom")])],"isStart":false});
            fillet(context, id + "F15", {"entities" : qUnion([Q0]), "radius" : 2 * mm, "tangentPropagation" : true, "allowEdgeOverflow" : false});
        }
        {
            var Q0;
            {var subQ0=sQuery(id+"F0.wireOp",EDGE,"E21.filletArc");var subQ1=sQuery(id+"F0.wireOp",EDGE,"E7");var subQ2=sQuery(id+"F0.wireOp",EDGE,"E6");var subQ3=sQuery(id+"F0.wireOp",EDGE,"E5");var subQ4=sQuery(id+"F0.wireOp",EDGE,"E4");var subQ5=sQuery(id+"F0.wireOp",EDGE,"E22.filletArc");var subQ6=sQuery(id+"F0.wireOp",EDGE,"E1.bottom");var subQ7=sQuery(id+"F0.wireOp",EDGE,"E1.right");var subQ8=sQuery(id+"F0.wireOp",EDGE,"E1.top");var subQ9=sQuery(id+"F0.wireOp",EDGE,"E1.left");var subQ10=sQuery(id+"F0.wireOp",EDGE,"E23.filletArc");var subQ11=sQuery(id+"F0.wireOp",EDGE,"E24.filletArc");Q0=makeQuery(id+"F2.boolean.opBoolean","SPLIT",FACE,{"disambiguationData":[TD([makeQuery(id+"F1.opExtrude","SWEPT_FACE",FACE,{"disambiguationData":[OSD([subQ6])]})])],"derivedFrom":makeQuery(id+"F1.opExtrude","CAP_FACE",FACE,{"disambiguationData":[OSD([subQ6,subQ8,subQ9,subQ7,subQ4,subQ3,subQ2,subQ1,subQ0,subQ5,subQ10,subQ11])],"isStart":true})});}
            var sketch = newSketch(context, id + "F16", { "sketchPlane" : qUnion([Q0])});
            skLineSegment(sketch, "E79", {"start": v(-33, 90) * mm, "end": v(33, 90) * mm});
            skLineSegment(sketch, "E80", {"start": v(-33, 90) * mm, "end": v(-15, 108) * mm});
            skLineSegment(sketch, "E81", {"start": v(33, 90) * mm, "end": v(15, 108) * mm});
            skLineSegment(sketch, "E82", {"start": v(-15, 108) * mm, "end": v(-15, 120) * mm});
            skLineSegment(sketch, "E83", {"start": v(15, 108) * mm, "end": v(15, 120) * mm});
            skArc(sketch, "E84", {"start": v(15, 120) * mm, "mid": v(0, 135) * mm, "end": v(-15, 120) * mm});
            skCircle(sketch, "E85", {"center": v(0, 120) * mm, "radius": 6 * mm});
            skLineSegment(sketch, "E86", {"start": v(0, 120) * mm, "end": v(0, 90) * mm, "construction": true});
            skLineSegment(sketch, "E87", {"start": v(-84.94, 0) * mm, "end": v(94.99, 0) * mm, "construction": true});
            skPoint(sketch, "E87.endSnap0", {"position": v(80, 0) * mm});
            skLineSegment(sketch, "E88.MirrorCS", {"start": v(0, -120) * mm, "end": v(0, -90) * mm, "construction": true});
            skLineSegment(sketch, "E89.MirrorCS", {"start": v(-33, -90) * mm, "end": v(33, -90) * mm});
            skLineSegment(sketch, "E90.MirrorCS", {"start": v(-33, -90) * mm, "end": v(-15, -108) * mm});
            skCircle(sketch, "E91.MirrorC", {"center": v(0, -120) * mm, "radius": 6 * mm});
            skLineSegment(sketch, "E92.MirrorCS", {"start": v(33, -90) * mm, "end": v(15, -108) * mm});
            skLineSegment(sketch, "E93.MirrorCS", {"start": v(-15, -108) * mm, "end": v(-15, -120) * mm});
            skLineSegment(sketch, "E94.MirrorCS", {"start": v(15, -108) * mm, "end": v(15, -120) * mm});
            skArc(sketch, "E95.MirrorCS", {"start": v(15, -120) * mm, "mid": v(0, -135) * mm, "end": v(-15, -120) * mm});
            skLineSegment(sketch, "E96", {"start": v(0, -141.5) * mm, "end": v(0, 141.87) * mm});
            skPoint(sketch, "E96.startSnap0", {"position": v(0, -90) * mm});
            skSolve(sketch);
        }
        {
            var Q0;
            Q0 = qSketchRegion(id + "F16", true);
            var Q1;
            Q1=makeQuery(id+"F16.imprint","IMPRINT",FACE,{"disambiguationData":[TD([[makeQuery(id+"F16.imprint","IMPRINT",EDGE,{"derivedFrom":makeQuery(id+"F1.opExtrude","CAP_EDGE",EDGE,{"disambiguationData":[OSD([sQuery(id+"F0.wireOp",EDGE,"E1.right")])],"isStart":true})}),1.0]])]});
            var Q2;
            Q2=makeQuery(id+"F16.imprint","IMPRINT",FACE,{"disambiguationData":[TD([[makeQuery(id+"F16.imprint","IMPRINT",EDGE,{"derivedFrom":makeQuery(id+"F1.opExtrude","CAP_EDGE",EDGE,{"disambiguationData":[OSD([sQuery(id+"F0.wireOp",EDGE,"E1.left")])],"isStart":true})}),-1.0]])]});
            var Q3;
            Q3=makeQuery(id+"F2.opExtrude","CAP_FACE",FACE,{"disambiguationData":[OSD([sQuery(id+"F0.wireOp",EDGE,"E12"),sQuery(id+"F0.wireOp",EDGE,"E13"),sQuery(id+"F0.wireOp",EDGE,"E14"),sQuery(id+"F0.wireOp",EDGE,"E15"),sQuery(id+"F0.wireOp",EDGE,"E17.filletArc"),sQuery(id+"F0.wireOp",EDGE,"E18.filletArc"),sQuery(id+"F0.wireOp",EDGE,"E19.filletArc"),sQuery(id+"F0.wireOp",EDGE,"E20.filletArc"),sQuery(id+"F0.wireOp",EDGE,"E25.0"),sQuery(id+"F0.wireOp",EDGE,"E25.1"),sQuery(id+"F0.wireOp",EDGE,"E25.2"),sQuery(id+"F0.wireOp",EDGE,"E25.3"),sQuery(id+"F0.wireOp",EDGE,"E25.4"),sQuery(id+"F0.wireOp",EDGE,"E25.5"),sQuery(id+"F0.wireOp",EDGE,"E25.6"),sQuery(id+"F0.wireOp",EDGE,"E25.7")])],"isStart":false});
            extrude(context, id + "F17", {"entities" : qUnion([Q0, Q1, Q2]), "endBound" : BoundingType.UP_TO_SURFACE, "endBoundEntityFace" : qUnion([Q3]), "depth" : 25 * mm});
        }
    });
